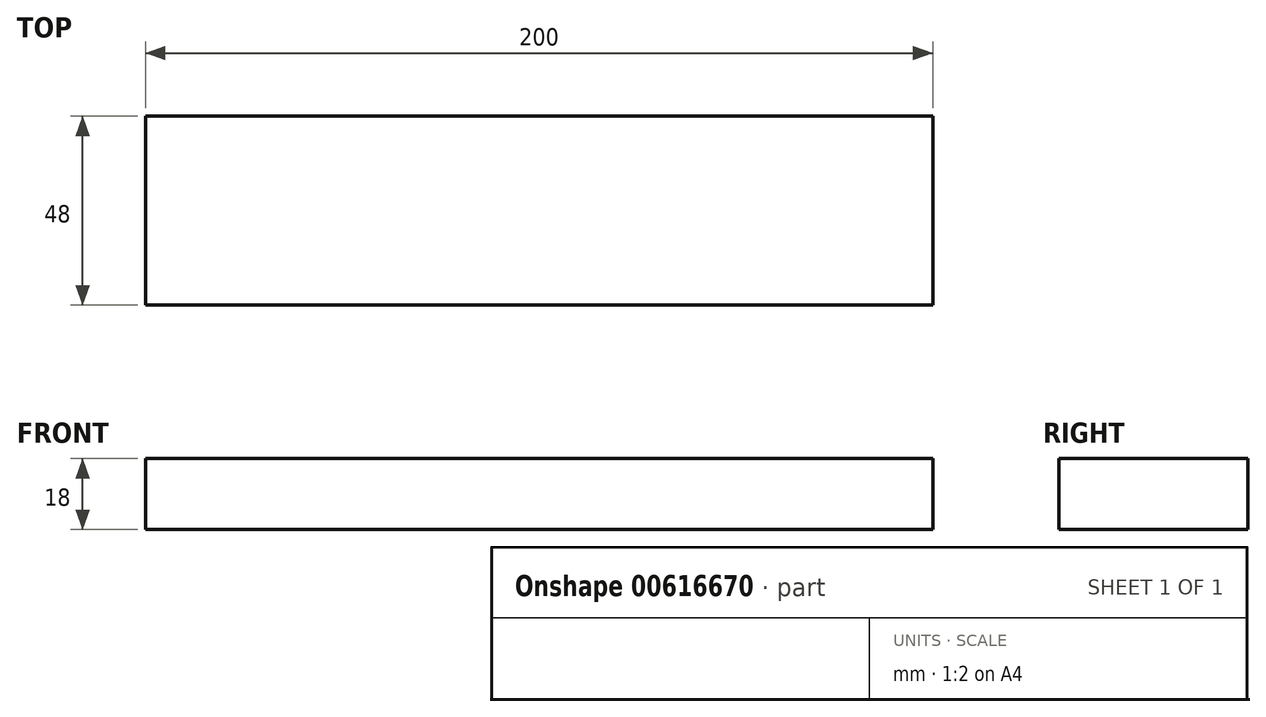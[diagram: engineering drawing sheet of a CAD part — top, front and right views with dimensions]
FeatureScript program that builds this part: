
annotation { "Feature Type Name" : "Feature", "Feature Type Description" : "" }
export const myFeature = defineFeature(function(context is Context, id is Id, definition is map)
    precondition{}
    {
        {
            var Q0;
            Q0=qCreatedBy(makeId("Top.planeOp"),FACE);
            var sketch = newSketch(context, id + "F0", { "sketchPlane" : qUnion([Q0])});
            skLineSegment(sketch, "E0.bottom", {"start": v(0, 0) * mm, "end": v(200, 0) * mm});
            skLineSegment(sketch, "E0.top", {"start": v(0, 48) * mm, "end": v(200, 48) * mm});
            skLineSegment(sketch, "E0.left", {"start": v(0, 0) * mm, "end": v(0, 48) * mm});
            skLineSegment(sketch, "E0.right", {"start": v(200, 0) * mm, "end": v(200, 48) * mm});
            skSolve(sketch);
        }
        {
            var Q0;
            Q0=makeQuery(id+"F0.imprint","IMPRINT",FACE,{"disambiguationData":[TD([[makeQuery(id+"F0.imprint","IMPRINT",EDGE,{"derivedFrom":sQuery(id+"F0.wireOp",EDGE,"E0.bottom")}),1.0]])]});
            extrude(context, id + "F1", {"entities" : qUnion([Q0]), "depth" : 18 * mm, "offsetDistance" : 25 * mm});
        }
    });
